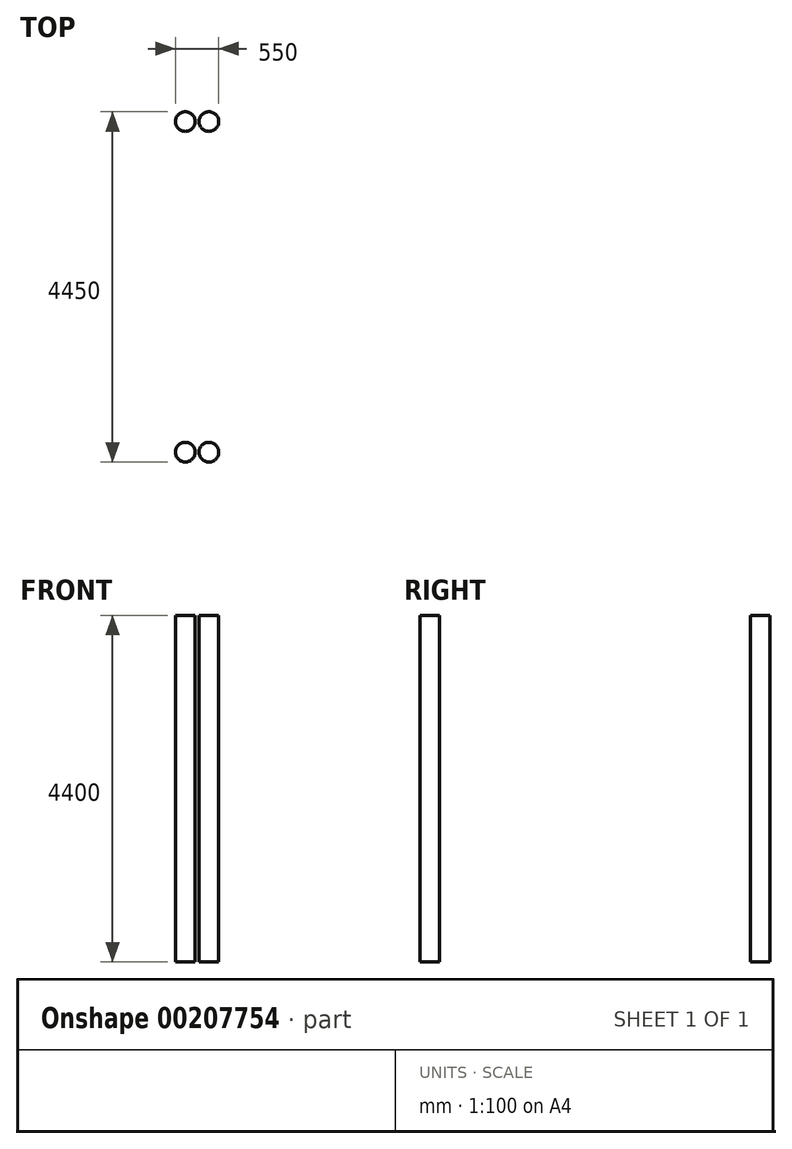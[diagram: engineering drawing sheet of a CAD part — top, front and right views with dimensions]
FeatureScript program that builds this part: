
annotation { "Feature Type Name" : "Feature", "Feature Type Description" : "" }
export const myFeature = defineFeature(function(context is Context, id is Id, definition is map)
    precondition{}
    {
        {
            var Q0;
            Q0=qCreatedBy(makeId("Top.planeOp"),FACE);
            cPlane(context, id + "F0", {"entities" : qUnion([Q0]), "cplaneType" : CPlaneType.OFFSET, "offset" : 2260 * mm, "width" : 150 * mm, "height" : 150 * mm});
        }
        {
            var Q0;
            Q0=qCreatedBy(id+"F0.planeOp",FACE);
            var sketch = newSketch(context, id + "F1", { "sketchPlane" : qUnion([Q0])});
            skCircle(sketch, "E0", {"center": v(150, -2100) * mm, "radius": 125 * mm});
            skSolve(sketch);
        }
        {
            var Q0;
            Q0=makeQuery(id+"F1.imprint","IMPRINT",FACE,{"disambiguationData":[TD([[makeQuery(id+"F1.imprint","IMPRINT",EDGE,{"derivedFrom":sQuery(id+"F1.wireOp",EDGE,"E0")}),1.0]])]});
            extrude(context, id + "F2", {"entities" : qUnion([Q0]), "depth" : 4400 * mm, "offsetDistance" : 25 * mm});
        }
        {
            var Q0;
            Q0=makeQuery(id+"F2.opExtrude","SWEPT_BODY",BODY,{"disambiguationData":[OSD([sQuery(id+"F1.wireOp",EDGE,"E0")])]});
            var Q1;
            Q1=qCreatedBy(makeId("Right.planeOp"),FACE);
            mirror(context, id + "F3", {"entities" : qUnion([Q0]), "mirrorPlane" : qUnion([Q1])});
        }
        {
            var Q0;
            Q0=makeQuery(id+"F2.opExtrude","SWEPT_BODY",BODY,{"disambiguationData":[OSD([sQuery(id+"F1.wireOp",EDGE,"E0")])]});
            var Q1;
            Q1=makeQuery(id+"F3.opPattern","COPY",BODY,{"derivedFrom":makeQuery(id+"F2.opExtrude","SWEPT_BODY",BODY,{"disambiguationData":[OSD([sQuery(id+"F1.wireOp",EDGE,"E0")])]}),"instanceName":"1"});
            var Q2;
            Q2=qCreatedBy(makeId("Front.planeOp"),FACE);
            mirror(context, id + "F4", {"entities" : qUnion([Q0, Q1]), "mirrorPlane" : qUnion([Q2])});
        }
    });
